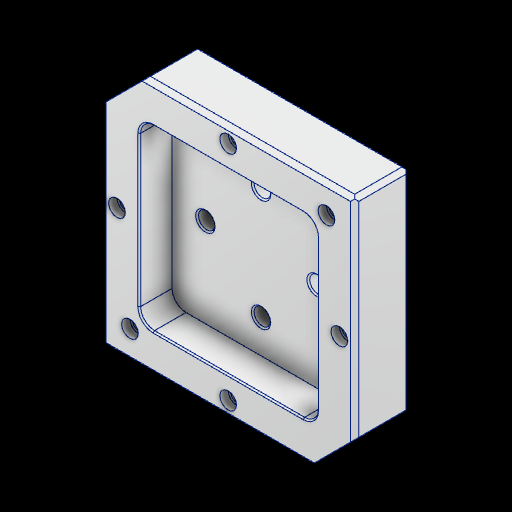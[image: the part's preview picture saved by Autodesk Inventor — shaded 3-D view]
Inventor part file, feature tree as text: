
AUTODESK INVENTOR PART (.ipt)
format: ipt  version: 2024 (Build 280153000, 153)  size: 236,544 bytes
history: native  units: mm
features: other x4, extrude x1, chamfer x1, sketch x1
ambient origin geometry x8: Origin, YZ Plane, XZ Plane, XY Plane, X Axis, Y Axis, Z Axis, Center Point
bodies: Body1 (feature_tree)
feature tree (7):
  other  "MicroPlast-MB-Layout.ipt"
  extrude  "Extrusion1"  Depth=10.0mm
  chamfer  "Fasen1"  [1 undecoded]
  other  "MP-Mould Mount B::MicroPlast-MB-Layout.ipt"
  other  "Bezeichnung1"
  sketch  "Skizze1"  dims[d0=10.0mm d2=0.4mm d3=0.0mm d4=0.0mm d5=0.5mm d6=2.0mm d7=45.0deg]
  other  "MP-Mould Mount B"
note: 1 required parameter value undecoded (feature->parameter linkage not recoverable at this tier; creation-order binding heuristic only, values carry confidence <= 0.55)
